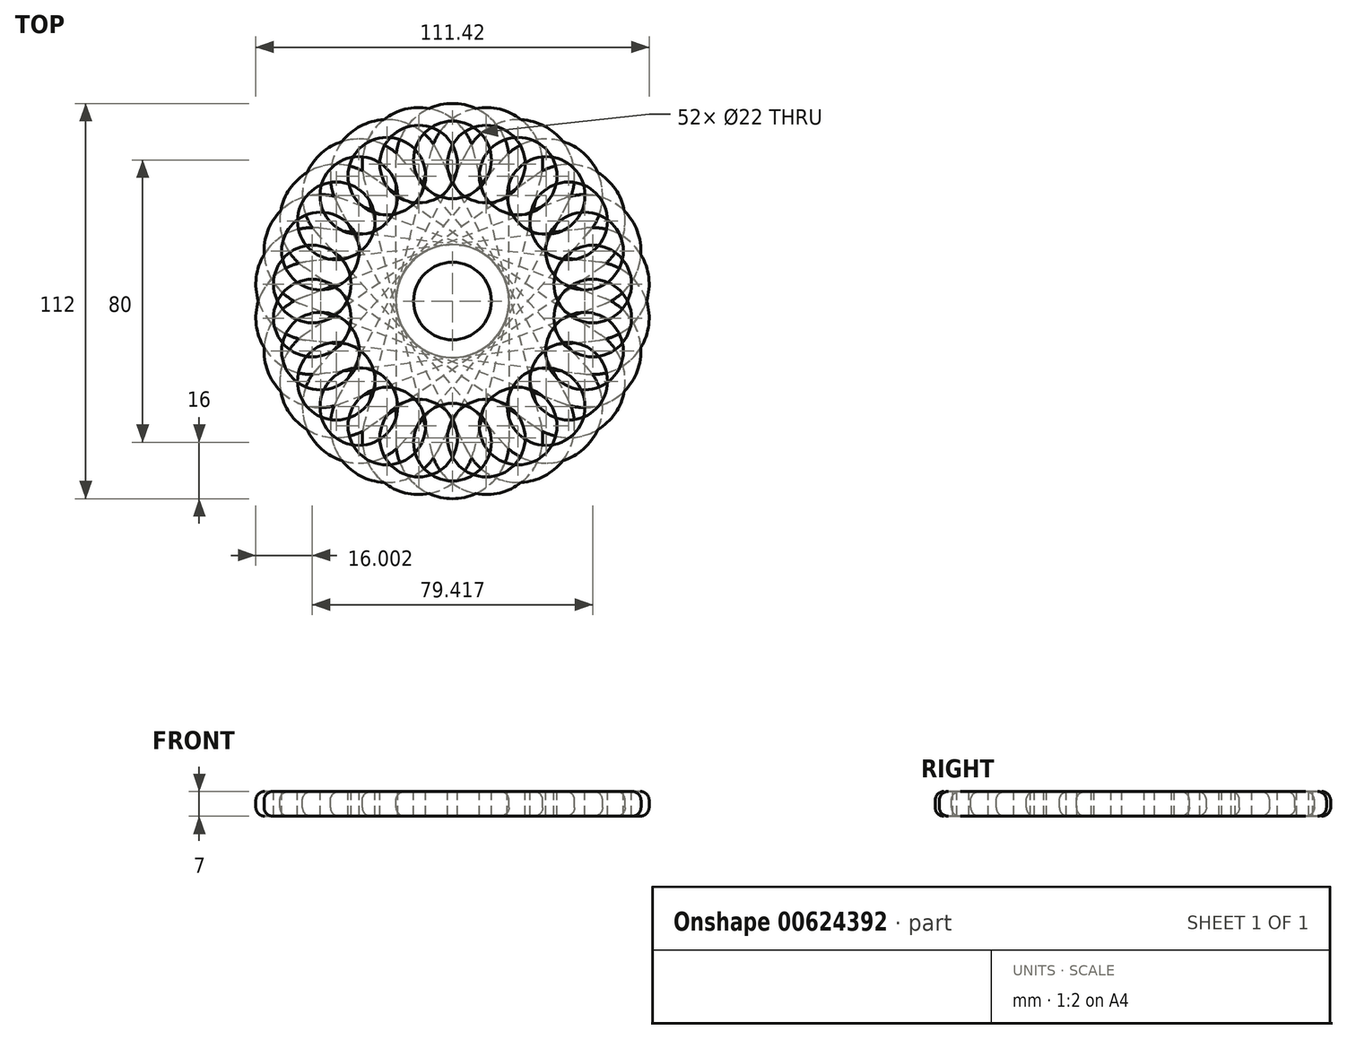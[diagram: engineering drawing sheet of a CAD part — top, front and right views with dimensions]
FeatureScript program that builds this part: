
annotation { "Feature Type Name" : "Feature", "Feature Type Description" : "" }
export const myFeature = defineFeature(function(context is Context, id is Id, definition is map)
    precondition{}
    {
        {
            var Q0;
            Q0=qCreatedBy(makeId("Top.planeOp"),FACE);
            var sketch = newSketch(context, id + "F0", { "sketchPlane" : qUnion([Q0])});
            skCircle(sketch, "E0", {"center": v(0, 0) * mm, "radius": 16 * mm});
            skCircle(sketch, "E1", {"center": v(0, -40) * mm, "radius": 16 * mm});
            skLineSegment(sketch, "E2", {"start": v(-16, 0) * mm, "end": v(-16, -40) * mm});
            skLineSegment(sketch, "E3", {"start": v(16, 0) * mm, "end": v(16, -40) * mm});
            skSolve(sketch);
        }
        {
            var Q0;
            Q0 = qSketchRegion(id + "F0", true);
            extrude(context, id + "F1", {"entities" : qUnion([Q0]), "oppositeDirection" : true, "depth" : 7 * mm, "offsetDistance" : 25 * mm});
        }
        {
            var Q0;
            Q0=qCreatedBy(makeId("Top.planeOp"),FACE);
            var sketch = newSketch(context, id + "F2", { "sketchPlane" : qUnion([Q0])});
            skCircle(sketch, "E4", {"center": v(0, 0) * mm, "radius": 11 * mm});
            skCircle(sketch, "E5", {"center": v(0, -40) * mm, "radius": 11 * mm});
            skSolve(sketch);
        }
        {
            var Q0;
            Q0 = qSketchRegion(id + "F2", true);
            extrude(context, id + "F3", {"entities" : qUnion([Q0]), "operationType" : NewBodyOperationType.REMOVE, "endBound" : BoundingType.THROUGH_ALL, "oppositeDirection" : true, "depth" : 25 * mm, "offsetDistance" : 25 * mm});
        }
        {
            var Q0;
            Q0=qCreatedBy(makeId("Front.planeOp"),FACE);
            var sketch = newSketch(context, id + "F4", { "sketchPlane" : qUnion([Q0])});
            skLineSegment(sketch, "E6", {"start": v(0, 0) * mm, "end": v(0, 49.07) * mm});
            skSolve(sketch);
        }
        {
            var Q0;
            Q0=makeQuery(id+"F1.opExtrude","CAP_EDGE",EDGE,{"disambiguationData":[OSD([sQuery(id+"F0.wireOp",EDGE,"E1")])],"isStart":true});
            fillet(context, id + "F5", {"entities" : qUnion([Q0]), "radius" : 2.5 * mm, "tangentPropagation" : true, "allowEdgeOverflow" : false});
        }
        {
            var Q0;
            Q0=makeQuery(id+"F1.opExtrude","CAP_EDGE",EDGE,{"disambiguationData":[OSD([sQuery(id+"F0.wireOp",EDGE,"E1")])],"isStart":false});
            fillet(context, id + "F6", {"entities" : qUnion([Q0]), "radius" : 2.5 * mm, "tangentPropagation" : true, "allowEdgeOverflow" : false});
        }
        {
            var Q0;
            Q0=makeQuery(id+"F1.opExtrude","SWEPT_BODY",BODY,{"disambiguationData":[OSD([sQuery(id+"F0.wireOp",EDGE,"E0"),sQuery(id+"F0.wireOp",EDGE,"E1"),sQuery(id+"F0.wireOp",EDGE,"E2"),sQuery(id+"F0.wireOp",EDGE,"E3"),sQuery(id+"F0.wireOp",EDGE,"sJ4zyRzt-Uacc-1mlX-siZe-S4dBVgNEyysm"),sQuery(id+"F0.wireOp",EDGE,"ZD5oWRBw-fFtJ-Ncvg-ARQk-uXfBSt53WtjU")])]});
            var Q1;
            Q1=sQuery(id+"F4.wireOp",EDGE,"E6");
            circularPattern(context, id + "F7", {"entities" : qUnion([Q0]), "axis" : qUnion([Q1]), "angle" : 360 * degree, "instanceCount" : 26, "equalSpace" : true});
        }
    });
